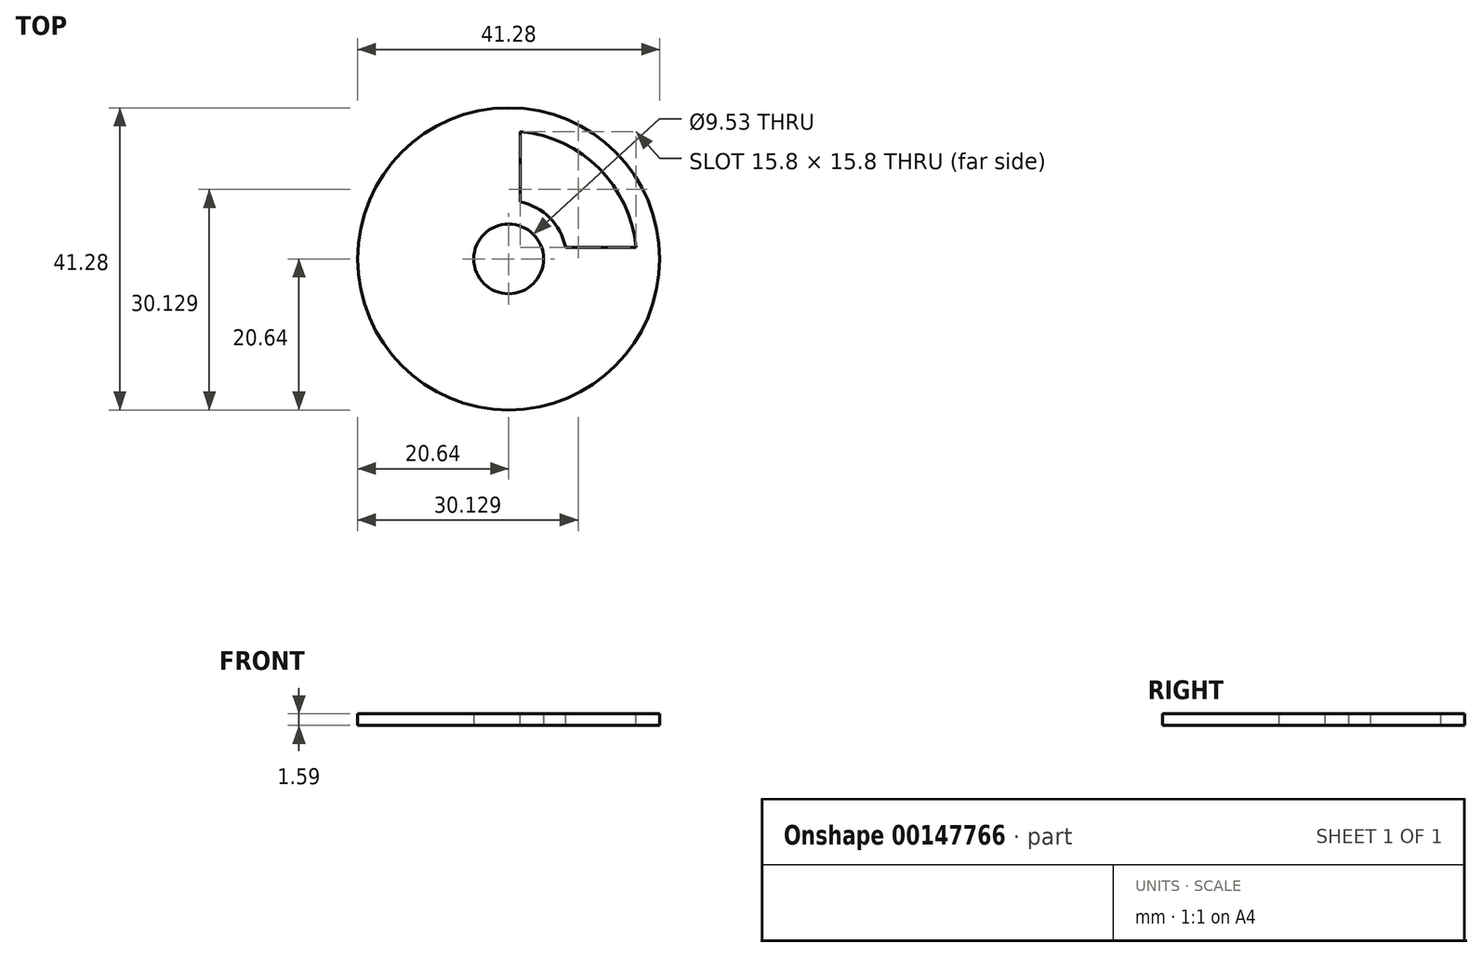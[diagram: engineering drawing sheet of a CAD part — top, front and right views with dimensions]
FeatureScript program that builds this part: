
annotation { "Feature Type Name" : "Feature", "Feature Type Description" : "" }
export const myFeature = defineFeature(function(context is Context, id is Id, definition is map)
    precondition{}
    {
        {
            var Q0;
            Q0=qCreatedBy(makeId("Top.planeOp"),FACE);
            var sketch = newSketch(context, id + "F0", { "sketchPlane" : qUnion([Q0])});
            skCircle(sketch, "E0", {"center": v(0, 0) * mm, "radius": 20.64 * mm});
            skCircle(sketch, "E1", {"center": v(0, 0) * mm, "radius": 4.76 * mm});
            skSolve(sketch);
        }
        {
            var Q0;
            Q0=qSketchRegion(id+"F0",true);
            extrude(context, id + "F1", {"entities" : qUnion([Q0]), "depth" : 1.59 * mm});
        }
        {
            var Q0;
            Q0=makeQuery(id+"F1.opExtrude","CAP_FACE",FACE,{"disambiguationData":[OSD([sQuery(id+"F0.wireOp",EDGE,"E0"),sQuery(id+"F0.wireOp",EDGE,"E1")])],"isStart":false});
            var sketch = newSketch(context, id + "F2", { "sketchPlane" : qUnion([Q0])});
            skLineSegment(sketch, "E2.bottom", {"start": v(-1.59, 7.78) * mm, "end": v(1.59, 7.78) * mm, "construction": true});
            skLineSegment(sketch, "E2.top", {"start": v(-1.59, 17.4) * mm, "end": v(1.59, 17.4) * mm, "construction": true});
            skLineSegment(sketch, "E2.left", {"start": v(-1.59, 7.78) * mm, "end": v(-1.59, 17.4) * mm, "construction": true});
            skLineSegment(sketch, "E2.right", {"start": v(1.59, 7.78) * mm, "end": v(1.59, 17.4) * mm});
            skLineSegment(sketch, "E3.bottom", {"start": v(7.78, 1.59) * mm, "end": v(17.4, 1.59) * mm});
            skLineSegment(sketch, "E3.top", {"start": v(7.78, -1.59) * mm, "end": v(17.4, -1.59) * mm, "construction": true});
            skLineSegment(sketch, "E3.left", {"start": v(7.78, 1.59) * mm, "end": v(7.78, -1.59) * mm, "construction": true});
            skLineSegment(sketch, "E3.right", {"start": v(17.4, 1.59) * mm, "end": v(17.4, -1.59) * mm, "construction": true});
            skArc(sketch, "E4", {"start": v(7.78, 1.59) * mm, "mid": v(5.61, 5.61) * mm, "end": v(1.59, 7.78) * mm});
            skArc(sketch, "E5", {"start": v(17.4, 1.59) * mm, "mid": v(12.35, 12.35) * mm, "end": v(1.59, 17.4) * mm});
            skLineSegment(sketch, "E6", {"start": v(0, 0) * mm, "end": v(0, 7.78) * mm, "construction": true});
            skLineSegment(sketch, "E7", {"start": v(0, 0) * mm, "end": v(7.78, 0) * mm, "construction": true});
            skSolve(sketch);
        }
        {
            var Q0;
            Q0=qSketchRegion(id+"F2",true);
            var Q1;
            Q1=makeQuery(id+"F1.opExtrude","CAP_FACE",FACE,{"disambiguationData":[OSD([sQuery(id+"F0.wireOp",EDGE,"E0"),sQuery(id+"F0.wireOp",EDGE,"E1")])],"isStart":true});
            extrude(context, id + "F3", {"entities" : qUnion([Q0]), "operationType" : NewBodyOperationType.REMOVE, "endBound" : BoundingType.UP_TO_SURFACE, "oppositeDirection" : true, "endBoundEntityFace" : qUnion([Q1]), "depth" : 25.4 * mm});
        }
    });
